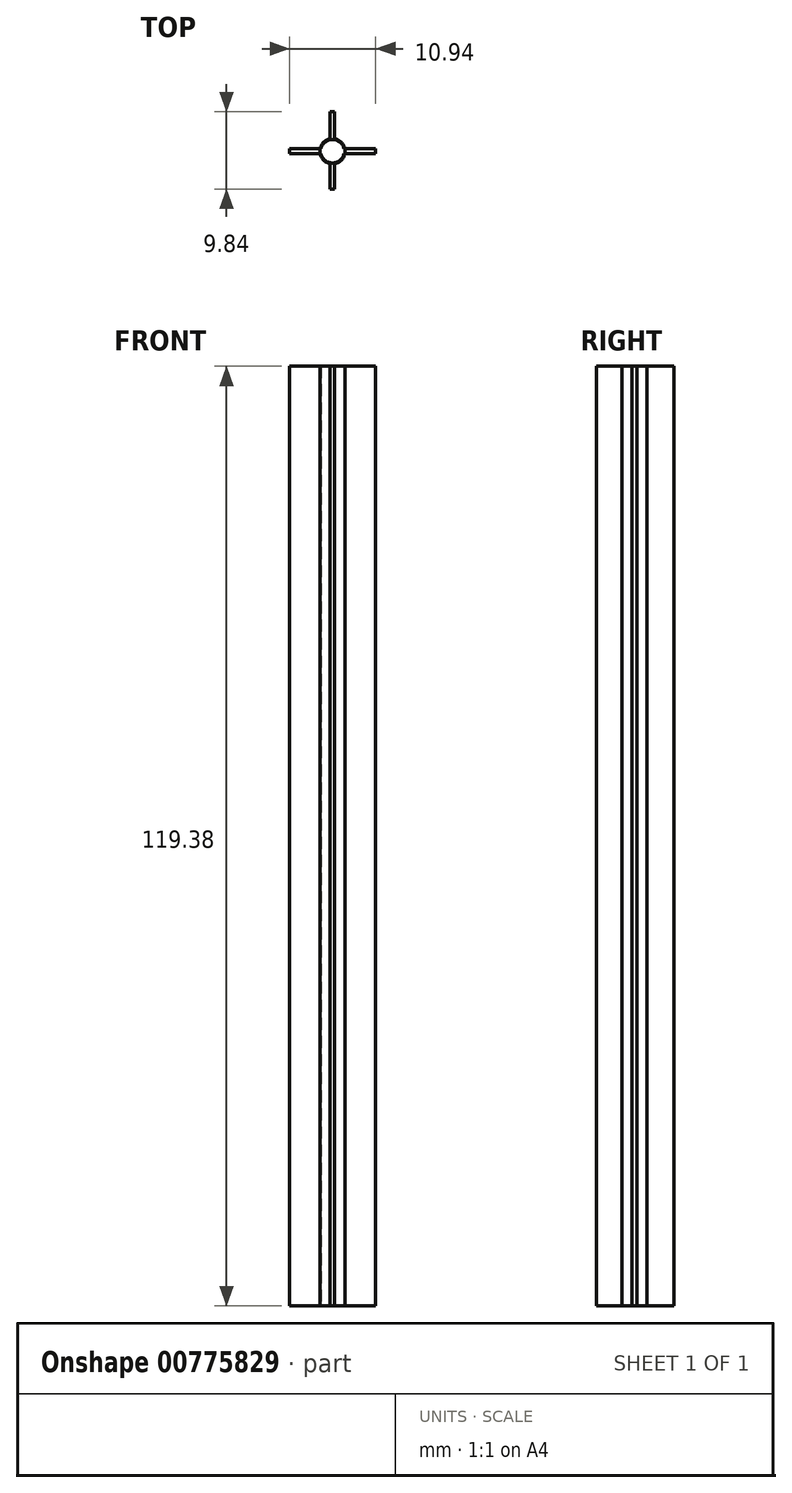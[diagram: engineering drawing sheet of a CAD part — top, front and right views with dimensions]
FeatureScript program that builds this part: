
annotation { "Feature Type Name" : "Feature", "Feature Type Description" : "" }
export const myFeature = defineFeature(function(context is Context, id is Id, definition is map)
    precondition{}
    {
        {
            var Q0;
            Q0=qCreatedBy(makeId("Top.planeOp"),FACE);
            var sketch = newSketch(context, id + "F0", { "sketchPlane" : qUnion([Q0])});
            skCircle(sketch, "E0", {"center": v(0, 0) * mm, "radius": 1.5 * mm});
            skLineSegment(sketch, "E1.bottom", {"start": v(-5.46, 0.33) * mm, "end": v(5.48, 0.33) * mm});
            skLineSegment(sketch, "E1.top", {"start": v(-5.46, -0.34) * mm, "end": v(5.48, -0.34) * mm});
            skLineSegment(sketch, "E1.left", {"start": v(-5.46, 0.33) * mm, "end": v(-5.46, -0.34) * mm});
            skLineSegment(sketch, "E1.right", {"start": v(5.48, 0.33) * mm, "end": v(5.48, -0.34) * mm});
            skLineSegment(sketch, "E2.bottom", {"start": v(-0.3, 5.03) * mm, "end": v(0.26, 5.03) * mm});
            skLineSegment(sketch, "E2.top", {"start": v(-0.3, -4.81) * mm, "end": v(0.26, -4.81) * mm});
            skLineSegment(sketch, "E2.left", {"start": v(-0.3, 5.03) * mm, "end": v(-0.3, -4.81) * mm});
            skLineSegment(sketch, "E2.right", {"start": v(0.26, 5.03) * mm, "end": v(0.26, -4.81) * mm});
            skCircle(sketch, "E3", {"center": v(0, 0) * mm, "radius": 1.6 * mm});
            skSolve(sketch);
        }
        {
            var Q0;
            {var subQ5=sQuery(id+"F0.wireOp",EDGE,"E2.bottom");Q0=makeQuery(id+"F0.imprint","IMPRINT",FACE,{"disambiguationData":[TD([[makeQuery(id+"F0.imprint","IMPRINT",EDGE,{"derivedFrom":subQ5}),-1.0]])]});}
            var Q1;
            {var subQ5=sQuery(id+"F0.wireOp",EDGE,"E1.left");Q1=makeQuery(id+"F0.imprint","IMPRINT",FACE,{"disambiguationData":[TD([[makeQuery(id+"F0.imprint","IMPRINT",EDGE,{"derivedFrom":subQ5}),1.0]])]});}
            var Q2;
            {var subQ5=sQuery(id+"F0.wireOp",EDGE,"E1.right");Q2=makeQuery(id+"F0.imprint","IMPRINT",FACE,{"disambiguationData":[TD([[makeQuery(id+"F0.imprint","IMPRINT",EDGE,{"derivedFrom":subQ5}),-1.0]])]});}
            var Q3;
            {var subQ5=sQuery(id+"F0.wireOp",EDGE,"E2.top");Q3=makeQuery(id+"F0.imprint","IMPRINT",FACE,{"disambiguationData":[TD([[makeQuery(id+"F0.imprint","IMPRINT",EDGE,{"derivedFrom":subQ5}),1.0]])]});}
            var Q4;
            {var subQ0=sQuery(id+"F0.wireOp",EDGE,"E2.right");var subQ1=sQuery(id+"F0.wireOp",EDGE,"E0");var subQ2=makeQuery(id+"F0.imprint","INTERSECT",VERTEX,{"disambiguationData":[OD(0.0)],"derivedFrom":[subQ1,subQ0]});Q4=makeQuery(id+"F0.imprint","IMPRINT",FACE,{"disambiguationData":[TD([[makeQuery(id+"F0.imprint","IMPRINT",EDGE,{"disambiguationData":[TD([[subQ2,1.0]])],"derivedFrom":subQ1}),-1.0]])]});}
            var Q5;
            {var subQ0=sQuery(id+"F0.wireOp",EDGE,"E2.right");var subQ1=sQuery(id+"F0.wireOp",EDGE,"E0");var subQ2=makeQuery(id+"F0.imprint","INTERSECT",VERTEX,{"disambiguationData":[OD(0.0)],"derivedFrom":[subQ1,subQ0]});Q5=makeQuery(id+"F0.imprint","IMPRINT",FACE,{"disambiguationData":[TD([[makeQuery(id+"F0.imprint","IMPRINT",EDGE,{"disambiguationData":[TD([[subQ2,-1.0]])],"derivedFrom":subQ1}),-1.0]])]});}
            var Q6;
            {var subQ0=sQuery(id+"F0.wireOp",EDGE,"E2.left");var subQ1=sQuery(id+"F0.wireOp",EDGE,"E0");var subQ2=makeQuery(id+"F0.imprint","INTERSECT",VERTEX,{"disambiguationData":[OD(0.0)],"derivedFrom":[subQ1,subQ0]});Q6=makeQuery(id+"F0.imprint","IMPRINT",FACE,{"disambiguationData":[TD([[makeQuery(id+"F0.imprint","IMPRINT",EDGE,{"disambiguationData":[TD([[subQ2,-1.0]])],"derivedFrom":subQ1}),-1.0]])]});}
            var Q7;
            {var subQ0=sQuery(id+"F0.wireOp",EDGE,"E1.bottom");var subQ1=sQuery(id+"F0.wireOp",EDGE,"E0");var subQ2=makeQuery(id+"F0.imprint","INTERSECT",VERTEX,{"disambiguationData":[OD(1.0)],"derivedFrom":[subQ1,subQ0]});Q7=makeQuery(id+"F0.imprint","IMPRINT",FACE,{"disambiguationData":[TD([[makeQuery(id+"F0.imprint","IMPRINT",EDGE,{"disambiguationData":[TD([[subQ2,-1.0]])],"derivedFrom":subQ1}),-1.0]])]});}
            var Q8;
            {var subQ0=sQuery(id+"F0.wireOp",EDGE,"E1.top");var subQ1=sQuery(id+"F0.wireOp",EDGE,"E0");var subQ2=makeQuery(id+"F0.imprint","INTERSECT",VERTEX,{"disambiguationData":[OD(0.0)],"derivedFrom":[subQ1,subQ0]});Q8=makeQuery(id+"F0.imprint","IMPRINT",FACE,{"disambiguationData":[TD([[makeQuery(id+"F0.imprint","IMPRINT",EDGE,{"disambiguationData":[TD([[subQ2,-1.0]])],"derivedFrom":subQ1}),-1.0]])]});}
            var Q9;
            {var subQ0=sQuery(id+"F0.wireOp",EDGE,"E2.left");var subQ1=sQuery(id+"F0.wireOp",EDGE,"E0");var subQ2=makeQuery(id+"F0.imprint","INTERSECT",VERTEX,{"disambiguationData":[OD(1.0)],"derivedFrom":[subQ1,subQ0]});Q9=makeQuery(id+"F0.imprint","IMPRINT",FACE,{"disambiguationData":[TD([[makeQuery(id+"F0.imprint","IMPRINT",EDGE,{"disambiguationData":[TD([[subQ2,-1.0]])],"derivedFrom":subQ1}),-1.0]])]});}
            var Q10;
            {var subQ0=sQuery(id+"F0.wireOp",EDGE,"E2.right");var subQ1=sQuery(id+"F0.wireOp",EDGE,"E0");var subQ2=makeQuery(id+"F0.imprint","INTERSECT",VERTEX,{"disambiguationData":[OD(1.0)],"derivedFrom":[subQ1,subQ0]});Q10=makeQuery(id+"F0.imprint","IMPRINT",FACE,{"disambiguationData":[TD([[makeQuery(id+"F0.imprint","IMPRINT",EDGE,{"disambiguationData":[TD([[subQ2,-1.0]])],"derivedFrom":subQ1}),-1.0]])]});}
            var Q11;
            {var subQ0=sQuery(id+"F0.wireOp",EDGE,"E1.bottom");var subQ1=sQuery(id+"F0.wireOp",EDGE,"E0");var subQ2=makeQuery(id+"F0.imprint","INTERSECT",VERTEX,{"disambiguationData":[OD(0.0)],"derivedFrom":[subQ1,subQ0]});Q11=makeQuery(id+"F0.imprint","IMPRINT",FACE,{"disambiguationData":[TD([[makeQuery(id+"F0.imprint","IMPRINT",EDGE,{"disambiguationData":[TD([[subQ2,1.0]])],"derivedFrom":subQ1}),-1.0]])]});}
            extrude(context, id + "F1", {"entities" : qUnion([Q0, Q1, Q2, Q3, Q4, Q5, Q6, Q7, Q8, Q9, Q10, Q11]), "depth" : 119.38 * mm, "offsetDistance" : 25.4 * mm});
        }
    });
